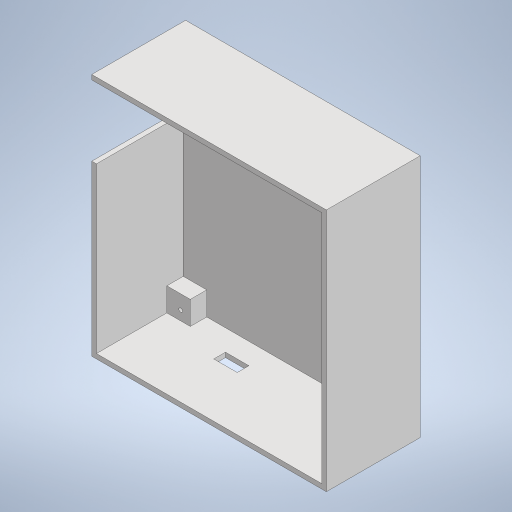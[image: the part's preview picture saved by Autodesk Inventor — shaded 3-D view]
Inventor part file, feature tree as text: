
AUTODESK INVENTOR PART (.ipt)
format: ipt  version: 2024.1 (Build 281209000, 209)  size: 278,528 bytes
history: native  units: in
note: dims shown in document units (in); Inventor stores cm internally (conversion verified against a paired STEP export)
features: extrude x7, sketch x7
ambient origin geometry x8: Origin, YZ Plane, XZ Plane, XY Plane, X Axis, Y Axis, Z Axis, Center Point
bodies: Solid1 (feature_tree)
feature tree (14):
  extrude  "Extrusion1"  Depth=4.0945in
  extrude  "Extrusion2"  Depth=0.0787in
  extrude  "Extrusion3"  Depth=0.0787in
  extrude  "Extrusion4"  Depth=1.4567in TaperAngle=0.0deg
  extrude  "Extrusion5"  Depth=0.3937in
  extrude  "Extrusion6"  Depth=0.3937in
  extrude  "Extrusion7"  Depth=0.3937in
  sketch  "Sketch1"  dims[d0=3.937in d1=4.0945in]
  sketch  "Sketch2"  dims[d2=1.5748in d3=0.0in d4=0.0787in]
  sketch  "Sketch3"  dims[d5=0.0787in d6=0.0787in]
  sketch  "Sketch4"  dims[d7=0.0787in d8=1.4567in d9=0.0in]
  sketch  "Sketch5"  dims[d10=0.3937in d11=0.3937in]
  sketch  "Sketch6"  dims[d12=0.3937in d13=0.3937in]
  sketch  "Sketch7"  dims[d14=0.3937in d15=0.3937in d16=0.3937in d17=0.3937in d18=0.2756in d19=0.0in d20=1.1811in d21=0.1969in d22=0.0in d23=0.7874in d24=0.2756in d25=0.0in d26=0.063in d27=0.063in d28=0.063in d29=0.063in d30=0.1575in d31=0.2313in d32=0.1575in d33=0.2313in d34=0.2313in d35=0.2313in d36=0.1575in d37=0.1575in d38=0.0in d39=0.0in d40=0.3937in d41=0.1969in d42=1.063in d43=0.3543in d44=0.0in d45=0.0in]
